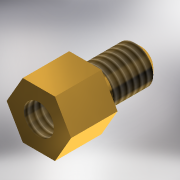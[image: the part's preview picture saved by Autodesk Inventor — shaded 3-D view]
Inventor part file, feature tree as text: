
AUTODESK INVENTOR PART (.ipt)
format: ipt  version: 2018.2 (Build 222227000, 227)  size: 137,216 bytes
history: native  units: mm
features: sketch x2, extrude x2, hole x1, thread x1, chamfer x1
ambient origin geometry x8: Origin, YZ Plane, XZ Plane, XY Plane, X Axis, Y Axis, Z Axis, Center Point
bodies: Solid1 (feature_tree)
feature tree (7):
  sketch  "Sketch1"  dims[d0=3.0mm d1=5.0mm d2=0.0mm]
  extrude  "Extrusion1"  Depth=5.0mm TaperAngle=0.0deg
  hole  "Hole2"  [1 undecoded]
  extrude  "Extrusion2"  Depth=6.0mm TaperAngle=0.0deg
  thread  "Thread1"  [1 undecoded]
  chamfer  "Chamfer1"  Distance=2.0mm Angle=45.0deg
  sketch  "Sketch3"  dims[d10=3.242mm d11=8.0mm d12=4.0mm d13=2.0mm d14=90.0deg d15=11.8mm d16=20.594885mm d17=4.0mm d18=6.0mm d19=0.0mm d20=5.0mm d21=0.0mm d22=0.7mm d23=2.0mm d24=45.0deg]
note: 2 required parameter values undecoded (feature->parameter linkage not recoverable at this tier; creation-order binding heuristic only, values carry confidence <= 0.55)
